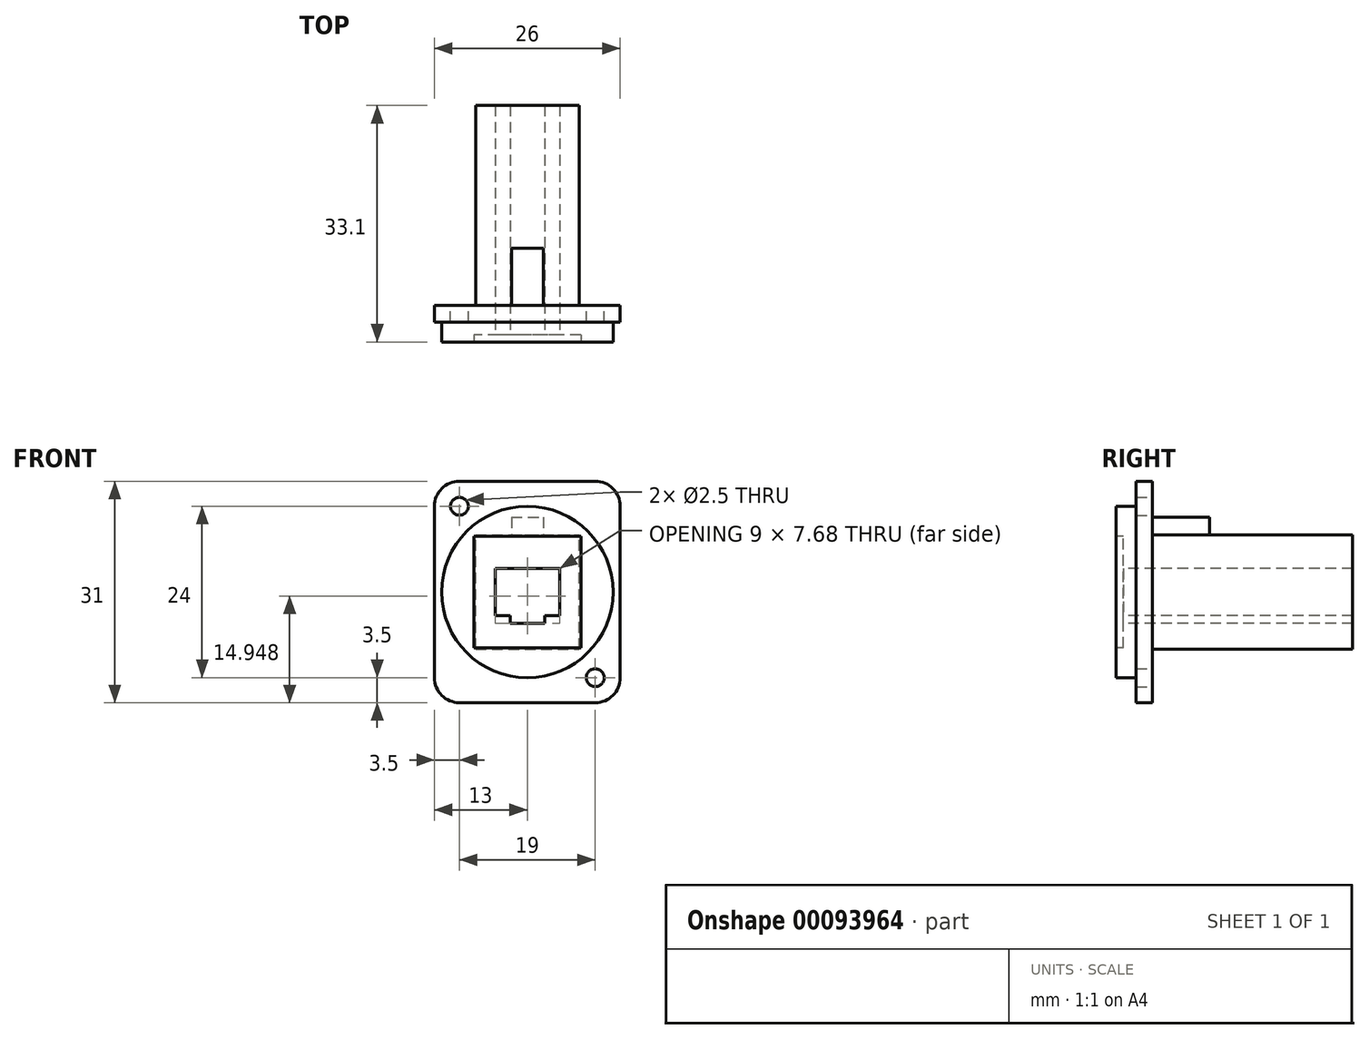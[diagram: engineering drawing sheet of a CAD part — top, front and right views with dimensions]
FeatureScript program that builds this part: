
annotation { "Feature Type Name" : "Feature", "Feature Type Description" : "" }
export const myFeature = defineFeature(function(context is Context, id is Id, definition is map)
    precondition{}
    {
        {
            var Q0;
            Q0=qCreatedBy(makeId("Front.planeOp"),FACE);
            var sketch = newSketch(context, id + "F0", { "sketchPlane" : qUnion([Q0])});
            skLineSegment(sketch, "E0.bottom", {"start": v(9.5, 15.5) * mm, "end": v(-9.5, 15.5) * mm});
            skLineSegment(sketch, "E0.top", {"start": v(9.5, -15.5) * mm, "end": v(-9.5, -15.5) * mm});
            skLineSegment(sketch, "E0.left", {"start": v(13, 12) * mm, "end": v(13, -12) * mm});
            skLineSegment(sketch, "E0.right", {"start": v(-13, 12) * mm, "end": v(-13, -12) * mm});
            skPoint(sketch, "E0.middle", {"position": v(0, 0) * mm});
            skCircle(sketch, "E1", {"center": v(-9.5, 12) * mm, "radius": 1.25 * mm});
            skCircle(sketch, "E2", {"center": v(9.5, -12) * mm, "radius": 1.25 * mm});
            skCircle(sketch, "E3", {"center": v(0, 0) * mm, "radius": 12 * mm});
            skPoint(sketch, "E4.visualSharp", {"position": v(-13, 15.5) * mm});
            skArc(sketch, "E4.filletArc", {"start": v(-9.5, 15.5) * mm, "mid": v(-11.97, 14.47) * mm, "end": v(-13, 12) * mm});
            skPoint(sketch, "E5.visualSharp", {"position": v(13, 15.5) * mm});
            skArc(sketch, "E5.filletArc", {"start": v(13, 12) * mm, "mid": v(11.97, 14.47) * mm, "end": v(9.5, 15.5) * mm});
            skPoint(sketch, "E6.visualSharp", {"position": v(13, -15.5) * mm});
            skArc(sketch, "E6.filletArc", {"start": v(9.5, -15.5) * mm, "mid": v(11.97, -14.47) * mm, "end": v(13, -12) * mm});
            skPoint(sketch, "E7.visualSharp", {"position": v(-13, -15.5) * mm});
            skArc(sketch, "E7.filletArc", {"start": v(-13, -12) * mm, "mid": v(-11.97, -14.47) * mm, "end": v(-9.5, -15.5) * mm});
            skSolve(sketch);
        }
        {
            var Q0;
            Q0=qSketchRegion(id+"F0",true);
            var Q1;
            Q1=makeQuery(id+"F0.imprint","IMPRINT",FACE,{"disambiguationData":[TD([[makeQuery(id+"F0.imprint","IMPRINT",EDGE,{"derivedFrom":sQuery(id+"F0.wireOp",EDGE,"E3")}),1.0]])]});
            extrude(context, id + "F1", {"entities" : qUnion([Q0, Q1]), "depth" : 2.3 * mm});
        }
        {
            var Q0;
            Q0=makeQuery(id+"F0.imprint","IMPRINT",FACE,{"disambiguationData":[TD([[makeQuery(id+"F0.imprint","IMPRINT",EDGE,{"derivedFrom":sQuery(id+"F0.wireOp",EDGE,"E3")}),1.0]])]});
            extrude(context, id + "F2", {"entities" : qUnion([Q0]), "operationType" : NewBodyOperationType.ADD, "depth" : 5.1 * mm});
        }
        {
            var Q0;
            Q0=makeQuery(id+"F2.opExtrude","CAP_FACE",FACE,{"disambiguationData":[OSD([sQuery(id+"F0.wireOp",EDGE,"E3")])],"isStart":false});
            var sketch = newSketch(context, id + "F3", { "sketchPlane" : qUnion([Q0])});
            skLineSegment(sketch, "E8.bottom", {"start": v(7.49, -7.82) * mm, "end": v(-7.49, -7.82) * mm});
            skLineSegment(sketch, "E8.top", {"start": v(7.49, 7.82) * mm, "end": v(-7.49, 7.82) * mm});
            skLineSegment(sketch, "E8.left", {"start": v(7.49, -7.82) * mm, "end": v(7.49, 7.82) * mm});
            skLineSegment(sketch, "E8.right", {"start": v(-7.49, -7.82) * mm, "end": v(-7.49, 7.82) * mm});
            skPoint(sketch, "E8.middle", {"position": v(0, 0) * mm});
            skLineSegment(sketch, "E9.bottom", {"start": v(4.5, 3.29) * mm, "end": v(-4.5, 3.29) * mm});
            skLineSegment(sketch, "E9.top", {"start": v(4.5, -3.29) * mm, "end": v(-4.5, -3.29) * mm});
            skLineSegment(sketch, "E9.left", {"start": v(4.5, 3.29) * mm, "end": v(4.5, -3.29) * mm});
            skLineSegment(sketch, "E9.right", {"start": v(-4.5, 3.29) * mm, "end": v(-4.5, -3.29) * mm});
            skLineSegment(sketch, "E10.bottom", {"start": v(2.42, -4.4) * mm, "end": v(-2.42, -4.4) * mm});
            skLineSegment(sketch, "E10.top", {"start": v(2.42, -2.18) * mm, "end": v(-2.42, -2.18) * mm});
            skLineSegment(sketch, "E10.left", {"start": v(2.42, -4.4) * mm, "end": v(2.42, -2.18) * mm});
            skLineSegment(sketch, "E10.right", {"start": v(-2.42, -4.4) * mm, "end": v(-2.42, -2.18) * mm});
            skPoint(sketch, "E10.middle", {"position": v(0, -3.29) * mm});
            skSolve(sketch);
        }
        {
            var Q0;
            Q0=makeQuery(id+"F3.imprint","IMPRINT",FACE,{"disambiguationData":[TD([[makeQuery(id+"F3.imprint","IMPRINT",EDGE,{"derivedFrom":sQuery(id+"F3.wireOp",EDGE,"E9.bottom")}),1.0]])]});
            var Q1;
            {var subQ5=sQuery(id+"F3.wireOp",EDGE,"E10.top");Q1=makeQuery(id+"F3.imprint","IMPRINT",FACE,{"disambiguationData":[TD([[makeQuery(id+"F3.imprint","IMPRINT",EDGE,{"derivedFrom":subQ5}),1.0]])]});}
            var Q2;
            {var subQ5=sQuery(id+"F3.wireOp",EDGE,"E10.bottom");Q2=makeQuery(id+"F3.imprint","IMPRINT",FACE,{"disambiguationData":[TD([[makeQuery(id+"F3.imprint","IMPRINT",EDGE,{"derivedFrom":subQ5}),-1.0]])]});}
            var Q3;
            Q3=makeQuery(id+"F3.imprint","IMPRINT",FACE,{"disambiguationData":[TD([[makeQuery(id+"F3.imprint","IMPRINT",EDGE,{"derivedFrom":sQuery(id+"F3.wireOp",EDGE,"E8.bottom")}),-1.0]])]});
            extrude(context, id + "F4", {"entities" : qUnion([Q0, Q1, Q2, Q3]), "operationType" : NewBodyOperationType.REMOVE, "oppositeDirection" : true, "depth" : 1 * mm});
        }
        {
            var Q0;
            Q0=makeQuery(id+"F3.imprint","IMPRINT",FACE,{"disambiguationData":[TD([[makeQuery(id+"F3.imprint","IMPRINT",EDGE,{"derivedFrom":sQuery(id+"F3.wireOp",EDGE,"E9.bottom")}),1.0]])]});
            var Q1;
            {var subQ5=sQuery(id+"F3.wireOp",EDGE,"E10.top");Q1=makeQuery(id+"F3.imprint","IMPRINT",FACE,{"disambiguationData":[TD([[makeQuery(id+"F3.imprint","IMPRINT",EDGE,{"derivedFrom":subQ5}),1.0]])]});}
            var Q2;
            {var subQ5=sQuery(id+"F3.wireOp",EDGE,"E10.bottom");Q2=makeQuery(id+"F3.imprint","IMPRINT",FACE,{"disambiguationData":[TD([[makeQuery(id+"F3.imprint","IMPRINT",EDGE,{"derivedFrom":subQ5}),-1.0]])]});}
            extrude(context, id + "F5", {"entities" : qUnion([Q0, Q1, Q2]), "operationType" : NewBodyOperationType.REMOVE, "oppositeDirection" : true, "depth" : 3 * mm});
        }
        {
            var Q0;
            Q0=makeQuery(id+"F1.opExtrude","CAP_FACE",FACE,{"disambiguationData":[OSD([sQuery(id+"F0.wireOp",EDGE,"E0.bottom"),sQuery(id+"F0.wireOp",EDGE,"E0.top"),sQuery(id+"F0.wireOp",EDGE,"E0.left"),sQuery(id+"F0.wireOp",EDGE,"E0.right"),sQuery(id+"F0.wireOp",EDGE,"E1"),sQuery(id+"F0.wireOp",EDGE,"E2"),sQuery(id+"F0.wireOp",EDGE,"E4.filletArc"),sQuery(id+"F0.wireOp",EDGE,"E5.filletArc"),sQuery(id+"F0.wireOp",EDGE,"E6.filletArc"),sQuery(id+"F0.wireOp",EDGE,"E7.filletArc")])],"isStart":true});
            var sketch = newSketch(context, id + "F6", { "sketchPlane" : qUnion([Q0])});
            skLineSegment(sketch, "E11.bottom", {"start": v(7.25, -8) * mm, "end": v(-7.25, -8) * mm});
            skLineSegment(sketch, "E11.top", {"start": v(7.25, 8) * mm, "end": v(-7.25, 8) * mm});
            skLineSegment(sketch, "E11.left", {"start": v(7.25, -8) * mm, "end": v(7.25, 8) * mm});
            skLineSegment(sketch, "E11.right", {"start": v(-7.25, -8) * mm, "end": v(-7.25, 8) * mm});
            skPoint(sketch, "E11.middle", {"position": v(0, 0) * mm});
            skPoint(sketch, "E12.middle", {"position": v(0, 8) * mm});
            skPoint(sketch, "E12.top.end.orphan", {"position": v(-3.1, 6.1) * mm});
            skPoint(sketch, "E13.orphan", {"position": v(3.1, 6.1) * mm});
            skPoint(sketch, "E12.bottom.end.orphan", {"position": v(-3.1, 9.9) * mm});
            skPoint(sketch, "E12.left.start.orphan", {"position": v(3.1, 9.9) * mm});
            skSolve(sketch);
        }
        {
            var Q0;
            Q0=qSketchRegion(id+"F6",true);
            extrude(context, id + "F7", {"entities" : qUnion([Q0]), "operationType" : NewBodyOperationType.ADD, "depth" : 28 * mm});
        }
        {
            var Q0;
            Q0=makeQuery(id+"F1.opExtrude","CAP_FACE",FACE,{"disambiguationData":[OSD([sQuery(id+"F0.wireOp",EDGE,"E0.bottom"),sQuery(id+"F0.wireOp",EDGE,"E0.top"),sQuery(id+"F0.wireOp",EDGE,"E0.left"),sQuery(id+"F0.wireOp",EDGE,"E0.right"),sQuery(id+"F0.wireOp",EDGE,"E1"),sQuery(id+"F0.wireOp",EDGE,"E2"),sQuery(id+"F0.wireOp",EDGE,"E4.filletArc"),sQuery(id+"F0.wireOp",EDGE,"E5.filletArc"),sQuery(id+"F0.wireOp",EDGE,"E6.filletArc"),sQuery(id+"F0.wireOp",EDGE,"E7.filletArc")])],"isStart":true});
            var sketch = newSketch(context, id + "F8", { "sketchPlane" : qUnion([Q0])});
            skLineSegment(sketch, "E14.bottom", {"start": v(2.22, 10.45) * mm, "end": v(-2.22, 10.45) * mm});
            skLineSegment(sketch, "E14.top", {"start": v(2.22, 5.55) * mm, "end": v(-2.22, 5.55) * mm});
            skLineSegment(sketch, "E14.left", {"start": v(2.22, 10.45) * mm, "end": v(2.22, 5.55) * mm});
            skLineSegment(sketch, "E14.right", {"start": v(-2.22, 10.45) * mm, "end": v(-2.22, 5.55) * mm});
            skPoint(sketch, "E14.middle", {"position": v(0, 8) * mm});
            skSolve(sketch);
        }
        {
            var Q0;
            Q0=qSketchRegion(id+"F8",true);
            extrude(context, id + "F9", {"entities" : qUnion([Q0]), "operationType" : NewBodyOperationType.ADD, "depth" : 8 * mm});
        }
        {
            var Q0;
            Q0=makeQuery(id+"F5.boolean.opBoolean","COPY",FACE,{"derivedFrom":makeQuery(id+"F5.opExtrude","CAP_FACE",FACE,{"disambiguationData":[OSD([sQuery(id+"F3.wireOp",EDGE,"E9.bottom"),sQuery(id+"F3.wireOp",EDGE,"E9.top"),sQuery(id+"F3.wireOp",EDGE,"E9.left"),sQuery(id+"F3.wireOp",EDGE,"E9.right"),sQuery(id+"F3.wireOp",EDGE,"E10.bottom"),sQuery(id+"F3.wireOp",EDGE,"E10.left"),sQuery(id+"F3.wireOp",EDGE,"E10.right")])],"isStart":false})});
            var Q1;
            Q1=makeQuery(id+"F1.opExtrude","SWEPT_BODY",BODY,{"disambiguationData":[OSD([sQuery(id+"F0.wireOp",EDGE,"E0.bottom"),sQuery(id+"F0.wireOp",EDGE,"E0.top"),sQuery(id+"F0.wireOp",EDGE,"E0.left"),sQuery(id+"F0.wireOp",EDGE,"E0.right"),sQuery(id+"F0.wireOp",EDGE,"E1"),sQuery(id+"F0.wireOp",EDGE,"E2"),sQuery(id+"F0.wireOp",EDGE,"E4.filletArc"),sQuery(id+"F0.wireOp",EDGE,"E5.filletArc"),sQuery(id+"F0.wireOp",EDGE,"E6.filletArc"),sQuery(id+"F0.wireOp",EDGE,"E7.filletArc")])]});
            extrude(context, id + "F10", {"entities" : qUnion([Q0]), "operationType" : NewBodyOperationType.REMOVE, "endBound" : BoundingType.UP_TO_BODY, "oppositeDirection" : true, "endBoundEntityBody" : qUnion([Q1]), "depth" : 25 * mm});
        }
    });
